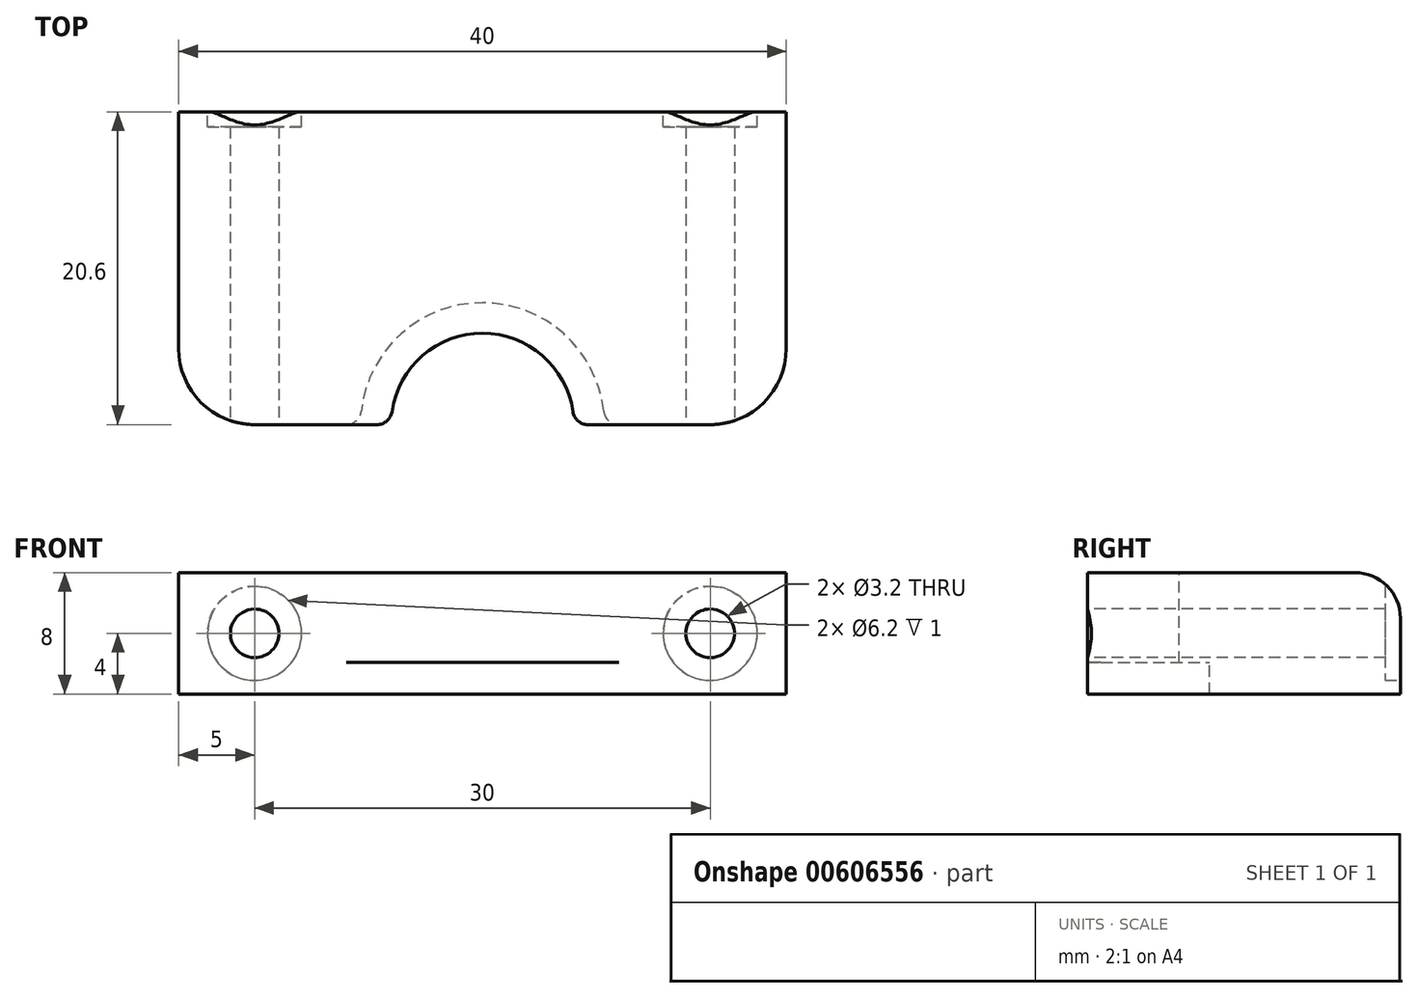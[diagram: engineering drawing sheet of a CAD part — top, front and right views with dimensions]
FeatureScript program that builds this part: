
annotation { "Feature Type Name" : "Feature", "Feature Type Description" : "" }
export const myFeature = defineFeature(function(context is Context, id is Id, definition is map)
    precondition{}
    {
        {
            var Q0;
            Q0=qCreatedBy(makeId("Top.planeOp"),FACE);
            var sketch = newSketch(context, id + "F0", { "sketchPlane" : qUnion([Q0])});
            skLineSegment(sketch, "E0.bottom", {"start": v(-20, 0) * mm, "end": v(-6.02, 0) * mm});
            skLineSegment(sketch, "E0.top", {"start": v(-20, 20.6) * mm, "end": v(20, 20.6) * mm});
            skLineSegment(sketch, "E0.left", {"start": v(-20, 0) * mm, "end": v(-20, 20.6) * mm});
            skLineSegment(sketch, "E0.right", {"start": v(20, 0) * mm, "end": v(20, 20.6) * mm});
            skArc(sketch, "E1", {"start": v(6.02, 0) * mm, "mid": v(0, 6.02) * mm, "end": v(-6.02, 0) * mm});
            skArc(sketch, "E2", {"start": v(8.03, 0) * mm, "mid": v(0, 8.03) * mm, "end": v(-8.03, 0) * mm});
            skLineSegment(sketch, "E3.trimOffspring", {"start": v(6.02, 0) * mm, "end": v(20, 0) * mm});
            skSolve(sketch);
        }
        {
            var Q0;
            Q0=makeQuery(id+"F0.imprint","IMPRINT",FACE,{"disambiguationData":[TD([[makeQuery(id+"F0.imprint","IMPRINT",EDGE,{"derivedFrom":sQuery(id+"F0.wireOp",EDGE,"E0.top")}),-1.0]])]});
            extrude(context, id + "F1", {"entities" : qUnion([Q0]), "oppositeDirection" : true, "depth" : (8) * mm, "offsetDistance" : 25 * mm});
        }
        {
            var Q0;
            {var subQ0=sQuery(id+"F0.wireOp",EDGE,"E1");Q0=makeQuery(id+"F0.imprint","IMPRINT",FACE,{"disambiguationData":[TD([[makeQuery(id+"F0.imprint","IMPRINT",EDGE,{"derivedFrom":subQ0}),-1.0]])]});}
            extrude(context, id + "F2", {"entities" : qUnion([Q0]), "operationType" : NewBodyOperationType.ADD, "oppositeDirection" : true, "depth" : 5.92 * mm, "offsetDistance" : 25 * mm});
        }
        {
            var Q0;
            Q0=makeQuery(id+"F1.opExtrude","CAP_EDGE",EDGE,{"disambiguationData":[OSD([sQuery(id+"F0.wireOp",EDGE,"E0.top")])],"isStart":true});
            fillet(context, id + "F3", {"entities" : qUnion([Q0]), "radius" : 3 * mm, "tangentPropagation" : true, "allowEdgeOverflow" : false});
        }
        {
            var Q0;
            Q0=makeQuery(id+"F1.opExtrude","SWEPT_EDGE",EDGE,{"disambiguationData":[OSD([sQuery(id+"F0.wireOp",EDGE,"E0.bottom"),sQuery(id+"F0.wireOp",EDGE,"E0.left")])]});
            var Q1;
            Q1=makeQuery(id+"F1.opExtrude","SWEPT_EDGE",EDGE,{"disambiguationData":[OSD([sQuery(id+"F0.wireOp",EDGE,"E0.right"),sQuery(id+"F0.wireOp",EDGE,"E3.trimOffspring")])]});
            fillet(context, id + "F4", {"entities" : qUnion([Q0, Q1]), "radius" : 5 * mm, "tangentPropagation" : true, "allowEdgeOverflow" : false});
        }
        {
            var Q0;
            {var subQ0=sQuery(id+"F0.wireOp",EDGE,"E0.bottom");Q0=makeQuery(id+"F2.boolean.opBoolean","MERGE",FACE,{"derivedFrom":[makeQuery(id+"F1.opExtrude","SWEPT_FACE",FACE,{"disambiguationData":[OSD([subQ0])]}),makeQuery(id+"F2.opExtrude","SWEPT_FACE",FACE,{"disambiguationData":[OSD([subQ0])]})]});}
            var sketch = newSketch(context, id + "F5", { "sketchPlane" : qUnion([Q0])});
            skLineSegment(sketch, "E4", {"start": v(-15, -4) * mm, "end": v(-6.02, -4) * mm, "construction": true});
            skLineSegment(sketch, "E5", {"start": v(-15, 0) * mm, "end": v(-15, -8) * mm, "construction": true});
            skCircle(sketch, "E6", {"center": v(-15, -4) * mm, "radius": 1.6 * mm});
            skSolve(sketch);
        }
        {
            var Q0;
            {var subQ0=sQuery(id+"F5.wireOp",EDGE,"E6");var subQ1=sQuery(id+"F0.wireOp",EDGE,"E0.bottom");var subQ2=makeQuery(id+"F4.opFillet","BLEND_EDGE",EDGE,{"blendedFrom":[makeQuery(id+"F1.opExtrude","SWEPT_EDGE",EDGE,{"disambiguationData":[OSD([subQ1,sQuery(id+"F0.wireOp",EDGE,"E0.left")])]}),makeQuery(id+"F2.boolean.opBoolean","MERGE",FACE,{"derivedFrom":[makeQuery(id+"F1.opExtrude","SWEPT_FACE",FACE,{"disambiguationData":[OSD([subQ1])]}),makeQuery(id+"F2.opExtrude","SWEPT_FACE",FACE,{"disambiguationData":[OSD([subQ1])]})]})],"blendedInto":[makeQuery(id+"F2.boolean.opBoolean","MERGE",FACE,{"derivedFrom":[makeQuery(id+"F1.opExtrude","SWEPT_FACE",FACE,{"disambiguationData":[OSD([subQ1])]}),makeQuery(id+"F2.opExtrude","SWEPT_FACE",FACE,{"disambiguationData":[OSD([subQ1])]})]})]});var subQ3=makeQuery(id+"F5.imprint","INTERSECT",VERTEX,{"disambiguationData":[OD(0.0)],"derivedFrom":[subQ2,subQ0]});Q0=makeQuery(id+"F5.imprint","IMPRINT",FACE,{"disambiguationData":[TD([[makeQuery(id+"F5.imprint","IMPRINT",EDGE,{"disambiguationData":[TD([[subQ3,-1.0]])],"derivedFrom":subQ0}),1.0]])]});}
            var Q1;
            {var subQ0=sQuery(id+"F5.wireOp",EDGE,"E6");var subQ1=sQuery(id+"F0.wireOp",EDGE,"E0.bottom");var subQ2=makeQuery(id+"F4.opFillet","BLEND_EDGE",EDGE,{"blendedFrom":[makeQuery(id+"F1.opExtrude","SWEPT_EDGE",EDGE,{"disambiguationData":[OSD([subQ1,sQuery(id+"F0.wireOp",EDGE,"E0.left")])]}),makeQuery(id+"F2.boolean.opBoolean","MERGE",FACE,{"derivedFrom":[makeQuery(id+"F1.opExtrude","SWEPT_FACE",FACE,{"disambiguationData":[OSD([subQ1])]}),makeQuery(id+"F2.opExtrude","SWEPT_FACE",FACE,{"disambiguationData":[OSD([subQ1])]})]})],"blendedInto":[makeQuery(id+"F2.boolean.opBoolean","MERGE",FACE,{"derivedFrom":[makeQuery(id+"F1.opExtrude","SWEPT_FACE",FACE,{"disambiguationData":[OSD([subQ1])]}),makeQuery(id+"F2.opExtrude","SWEPT_FACE",FACE,{"disambiguationData":[OSD([subQ1])]})]})]});var subQ3=makeQuery(id+"F5.imprint","INTERSECT",VERTEX,{"disambiguationData":[OD(0.0)],"derivedFrom":[subQ2,subQ0]});Q1=makeQuery(id+"F5.imprint","IMPRINT",FACE,{"disambiguationData":[TD([[makeQuery(id+"F5.imprint","IMPRINT",EDGE,{"disambiguationData":[TD([[subQ3,1.0]])],"derivedFrom":subQ0}),1.0]])]});}
            extrude(context, id + "F6", {"entities" : qUnion([Q0, Q1]), "operationType" : NewBodyOperationType.REMOVE, "endBound" : BoundingType.THROUGH_ALL, "oppositeDirection" : true, "depth" : 25 * mm, "offsetDistance" : 25 * mm});
        }
        {
            var Q0;
            {var subQ0=sQuery(id+"F0.wireOp",EDGE,"E3.trimOffspring");Q0=makeQuery(id+"F2.boolean.opBoolean","MERGE",FACE,{"derivedFrom":[makeQuery(id+"F1.opExtrude","SWEPT_FACE",FACE,{"disambiguationData":[OSD([subQ0])]}),makeQuery(id+"F2.opExtrude","SWEPT_FACE",FACE,{"disambiguationData":[OSD([subQ0])]})]});}
            var sketch = newSketch(context, id + "F7", { "sketchPlane" : qUnion([Q0])});
            skLineSegment(sketch, "E7", {"start": v(20.05, -4) * mm, "end": v(6.9, -4) * mm, "construction": true});
            skPoint(sketch, "E7.startSnap0", {"position": v(15, -4) * mm});
            skLineSegment(sketch, "E8", {"start": v(15, 0) * mm, "end": v(15, -7.94) * mm, "construction": true});
            skCircle(sketch, "E9", {"center": v(15, -4) * mm, "radius": 1.6 * mm});
            skSolve(sketch);
        }
        {
            var Q0;
            {var subQ0=sQuery(id+"F7.wireOp",EDGE,"E9");var subQ1=sQuery(id+"F0.wireOp",EDGE,"E3.trimOffspring");var subQ2=makeQuery(id+"F4.opFillet","BLEND_EDGE",EDGE,{"blendedFrom":[makeQuery(id+"F1.opExtrude","SWEPT_EDGE",EDGE,{"disambiguationData":[OSD([sQuery(id+"F0.wireOp",EDGE,"E0.right"),subQ1])]}),makeQuery(id+"F2.boolean.opBoolean","MERGE",FACE,{"derivedFrom":[makeQuery(id+"F1.opExtrude","SWEPT_FACE",FACE,{"disambiguationData":[OSD([subQ1])]}),makeQuery(id+"F2.opExtrude","SWEPT_FACE",FACE,{"disambiguationData":[OSD([subQ1])]})]})],"blendedInto":[makeQuery(id+"F2.boolean.opBoolean","MERGE",FACE,{"derivedFrom":[makeQuery(id+"F1.opExtrude","SWEPT_FACE",FACE,{"disambiguationData":[OSD([subQ1])]}),makeQuery(id+"F2.opExtrude","SWEPT_FACE",FACE,{"disambiguationData":[OSD([subQ1])]})]})]});var subQ3=makeQuery(id+"F7.imprint","INTERSECT",VERTEX,{"disambiguationData":[OD(0.0)],"derivedFrom":[subQ2,subQ0]});Q0=makeQuery(id+"F7.imprint","IMPRINT",FACE,{"disambiguationData":[TD([[makeQuery(id+"F7.imprint","IMPRINT",EDGE,{"disambiguationData":[TD([[subQ3,1.0]])],"derivedFrom":subQ0}),1.0]])]});}
            var Q1;
            {var subQ0=sQuery(id+"F7.wireOp",EDGE,"E9");var subQ1=sQuery(id+"F0.wireOp",EDGE,"E3.trimOffspring");var subQ2=makeQuery(id+"F4.opFillet","BLEND_EDGE",EDGE,{"blendedFrom":[makeQuery(id+"F1.opExtrude","SWEPT_EDGE",EDGE,{"disambiguationData":[OSD([sQuery(id+"F0.wireOp",EDGE,"E0.right"),subQ1])]}),makeQuery(id+"F2.boolean.opBoolean","MERGE",FACE,{"derivedFrom":[makeQuery(id+"F1.opExtrude","SWEPT_FACE",FACE,{"disambiguationData":[OSD([subQ1])]}),makeQuery(id+"F2.opExtrude","SWEPT_FACE",FACE,{"disambiguationData":[OSD([subQ1])]})]})],"blendedInto":[makeQuery(id+"F2.boolean.opBoolean","MERGE",FACE,{"derivedFrom":[makeQuery(id+"F1.opExtrude","SWEPT_FACE",FACE,{"disambiguationData":[OSD([subQ1])]}),makeQuery(id+"F2.opExtrude","SWEPT_FACE",FACE,{"disambiguationData":[OSD([subQ1])]})]})]});var subQ3=makeQuery(id+"F7.imprint","INTERSECT",VERTEX,{"disambiguationData":[OD(0.0)],"derivedFrom":[subQ2,subQ0]});Q1=makeQuery(id+"F7.imprint","IMPRINT",FACE,{"disambiguationData":[TD([[makeQuery(id+"F7.imprint","IMPRINT",EDGE,{"disambiguationData":[TD([[subQ3,-1.0]])],"derivedFrom":subQ0}),1.0]])]});}
            extrude(context, id + "F8", {"entities" : qUnion([Q0, Q1]), "operationType" : NewBodyOperationType.REMOVE, "endBound" : BoundingType.THROUGH_ALL, "oppositeDirection" : true, "depth" : 25 * mm, "offsetDistance" : 25 * mm});
        }
        {
            var Q0;
            Q0=makeQuery(id+"F1.opExtrude","SWEPT_EDGE",EDGE,{"disambiguationData":[OSD([sQuery(id+"F0.wireOp",EDGE,"E0.bottom"),sQuery(id+"F0.wireOp",EDGE,"E2")])]});
            var Q1;
            Q1=makeQuery(id+"F2.opExtrude","SWEPT_EDGE",EDGE,{"disambiguationData":[OSD([sQuery(id+"F0.wireOp",EDGE,"E0.bottom"),sQuery(id+"F0.wireOp",EDGE,"E1")])]});
            var Q2;
            Q2=makeQuery(id+"F2.opExtrude","SWEPT_EDGE",EDGE,{"disambiguationData":[OSD([sQuery(id+"F0.wireOp",EDGE,"E1"),sQuery(id+"F0.wireOp",EDGE,"E3.trimOffspring")])]});
            var Q3;
            Q3=makeQuery(id+"F1.opExtrude","SWEPT_EDGE",EDGE,{"disambiguationData":[OSD([sQuery(id+"F0.wireOp",EDGE,"E2"),sQuery(id+"F0.wireOp",EDGE,"E3.trimOffspring")])]});
            fillet(context, id + "F9", {"entities" : qUnion([Q0, Q1, Q2, Q3]), "radius" : 1 * mm, "tangentPropagation" : true, "allowEdgeOverflow" : false});
        }
        {
            var Q0;
            Q0=makeQuery(id+"F1.opExtrude","SWEPT_FACE",FACE,{"disambiguationData":[OSD([sQuery(id+"F0.wireOp",EDGE,"E0.top")])]});
            var sketch = newSketch(context, id + "F10", { "sketchPlane" : qUnion([Q0])});
            skCircle(sketch, "E10", {"center": v(-15, -4) * mm, "radius": 3.1 * mm});
            skCircle(sketch, "E11", {"center": v(15, -4) * mm, "radius": 3.1 * mm});
            skSolve(sketch);
        }
        {
            var Q0;
            {var subQ1=sQuery(id+"F0.wireOp",EDGE,"E0.top");var subQ2=makeQuery(id+"F1.opExtrude","SWEPT_FACE",FACE,{"disambiguationData":[OSD([subQ1])]});var subQ4=makeQuery(id+"F8.opExtrude","SWEPT_FACE",FACE,{"disambiguationData":[OSD([sQuery(id+"F7.wireOp",EDGE,"E9")])]});var subQ12=makeQuery(id+"F8.boolean.opBoolean","INTERSECT",EDGE,{"derivedFrom":[subQ2,subQ4]});Q0=makeQuery(id+"F10.imprint","IMPRINT",FACE,{"disambiguationData":[TD([[makeQuery(id+"F10.imprint","IMPRINT",EDGE,{"derivedFrom":subQ12}),-1.0]])]});}
            var Q1;
            {var subQ1=sQuery(id+"F0.wireOp",EDGE,"E0.top");var subQ2=makeQuery(id+"F1.opExtrude","SWEPT_FACE",FACE,{"disambiguationData":[OSD([subQ1])]});var subQ4=makeQuery(id+"F8.opExtrude","SWEPT_FACE",FACE,{"disambiguationData":[OSD([sQuery(id+"F7.wireOp",EDGE,"E9")])]});var subQ12=makeQuery(id+"F8.boolean.opBoolean","INTERSECT",EDGE,{"derivedFrom":[subQ2,subQ4]});Q1=makeQuery(id+"F10.imprint","IMPRINT",FACE,{"disambiguationData":[TD([[makeQuery(id+"F10.imprint","IMPRINT",EDGE,{"derivedFrom":subQ12}),1.0]])]});}
            var Q2;
            {var subQ1=sQuery(id+"F0.wireOp",EDGE,"E0.top");var subQ2=makeQuery(id+"F1.opExtrude","SWEPT_FACE",FACE,{"disambiguationData":[OSD([subQ1])]});var subQ4=makeQuery(id+"F6.opExtrude","SWEPT_FACE",FACE,{"disambiguationData":[OSD([sQuery(id+"F5.wireOp",EDGE,"E6")])]});var subQ10=makeQuery(id+"F6.boolean.opBoolean","INTERSECT",EDGE,{"derivedFrom":[subQ2,subQ4]});Q2=makeQuery(id+"F10.imprint","IMPRINT",FACE,{"disambiguationData":[TD([[makeQuery(id+"F10.imprint","IMPRINT",EDGE,{"derivedFrom":subQ10}),-1.0]])]});}
            var Q3;
            {var subQ1=sQuery(id+"F0.wireOp",EDGE,"E0.top");var subQ2=makeQuery(id+"F1.opExtrude","SWEPT_FACE",FACE,{"disambiguationData":[OSD([subQ1])]});var subQ4=makeQuery(id+"F6.opExtrude","SWEPT_FACE",FACE,{"disambiguationData":[OSD([sQuery(id+"F5.wireOp",EDGE,"E6")])]});var subQ10=makeQuery(id+"F6.boolean.opBoolean","INTERSECT",EDGE,{"derivedFrom":[subQ2,subQ4]});Q3=makeQuery(id+"F10.imprint","IMPRINT",FACE,{"disambiguationData":[TD([[makeQuery(id+"F10.imprint","IMPRINT",EDGE,{"derivedFrom":subQ10}),1.0]])]});}
            extrude(context, id + "F11", {"entities" : qUnion([Q0, Q1, Q2, Q3]), "operationType" : NewBodyOperationType.REMOVE, "oppositeDirection" : true, "depth" : 1 * mm, "offsetDistance" : 25 * mm});
        }
    });
